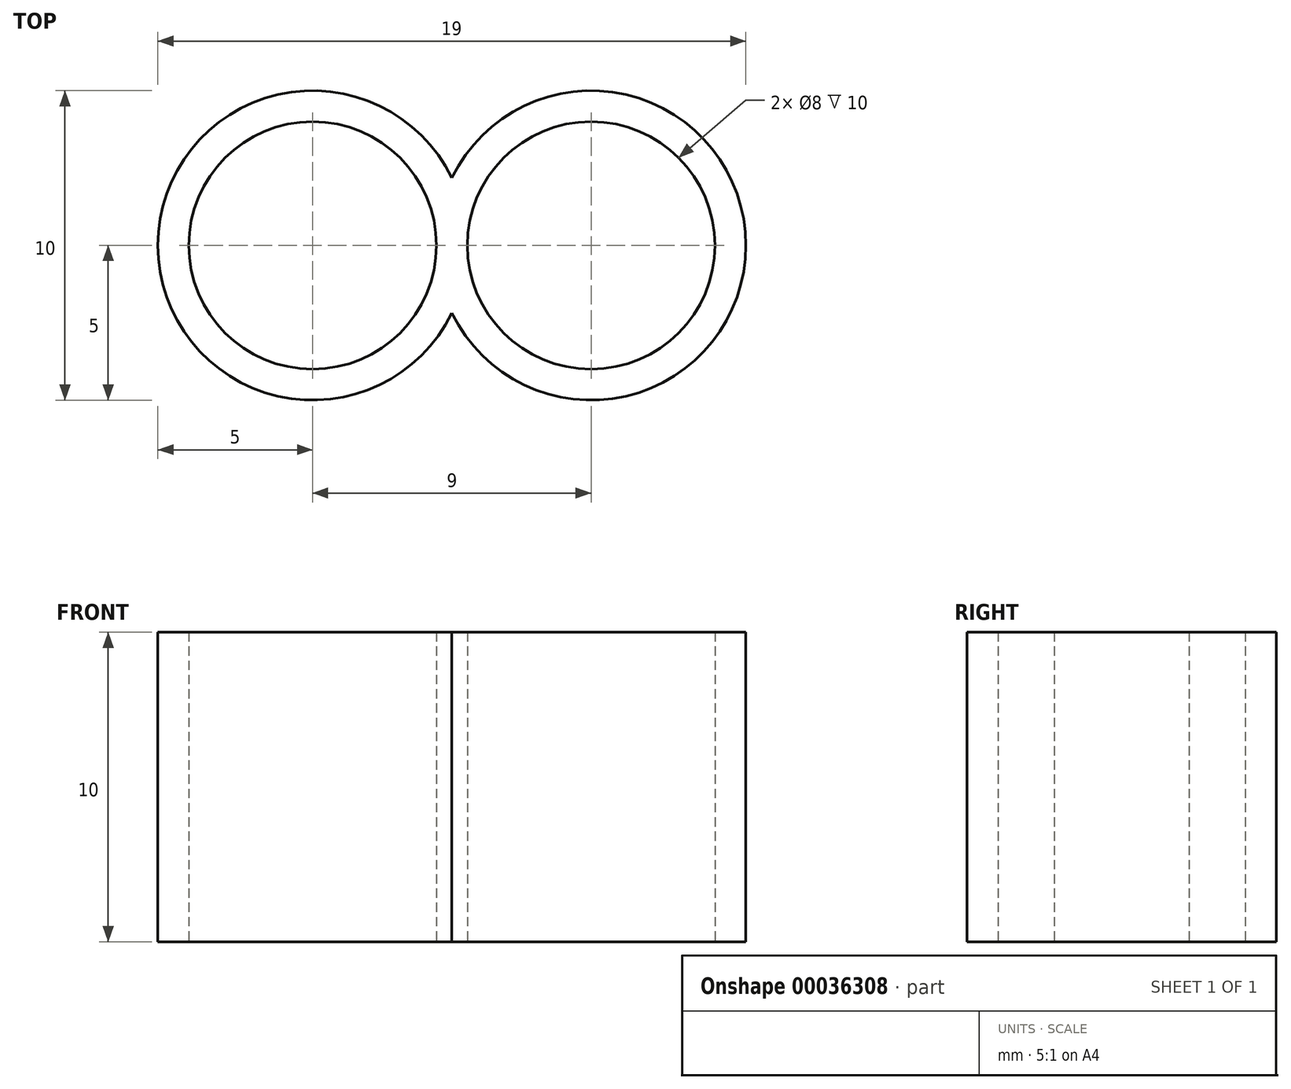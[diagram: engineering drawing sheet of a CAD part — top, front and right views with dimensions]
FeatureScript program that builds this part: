
annotation { "Feature Type Name" : "Feature", "Feature Type Description" : "" }
export const myFeature = defineFeature(function(context is Context, id is Id, definition is map)
    precondition{}
    {
        {
            var Q0;
            Q0=qCreatedBy(makeId("Top.planeOp"),FACE);
            var sketch = newSketch(context, id + "F0", { "sketchPlane" : qUnion([Q0])});
            skCircle(sketch, "E0", {"center": v(0, 0) * mm, "radius": 5 * mm});
            skCircle(sketch, "E1", {"center": v(9, 0) * mm, "radius": 5 * mm});
            skCircle(sketch, "E2", {"center": v(0, 0) * mm, "radius": 4 * mm});
            skCircle(sketch, "E3", {"center": v(9, 0) * mm, "radius": 4 * mm});
            skLineSegment(sketch, "E4", {"start": v(5, 0) * mm, "end": v(4, 0) * mm, "construction": true});
            skLineSegment(sketch, "E5", {"start": v(4, 0) * mm, "end": v(0, 0) * mm, "construction": true});
            skLineSegment(sketch, "E6", {"start": v(4, 0) * mm, "end": v(5, 0) * mm, "construction": true});
            skLineSegment(sketch, "E7", {"start": v(5, 0) * mm, "end": v(9, 0) * mm, "construction": true});
            skSolve(sketch);
        }
        {
            var Q0;
            Q0=makeQuery(id+"F0.imprint","IMPRINT",FACE,{"disambiguationData":[TD([[makeQuery(id+"F0.imprint","IMPRINT",EDGE,{"derivedFrom":sQuery(id+"F0.wireOp",EDGE,"E1")}),1.0]])]});
            var Q1;
            {var subQ0=sQuery(id+"F0.wireOp",EDGE,"E2");Q1=makeQuery(id+"F0.imprint","IMPRINT",FACE,{"disambiguationData":[TD([[makeQuery(id+"F0.imprint","IMPRINT",EDGE,{"derivedFrom":subQ0}),-1.0]])]});}
            var Q2;
            {var subQ4=sQuery(id+"F0.wireOp",EDGE,"E3");Q2=makeQuery(id+"F0.imprint","IMPRINT",FACE,{"disambiguationData":[TD([[makeQuery(id+"F0.imprint","IMPRINT",EDGE,{"derivedFrom":subQ4}),-1.0]])]});}
            extrude(context, id + "F1", {"entities" : qUnion([Q0, Q1, Q2]), "depth" : 10 * mm});
        }
    });
